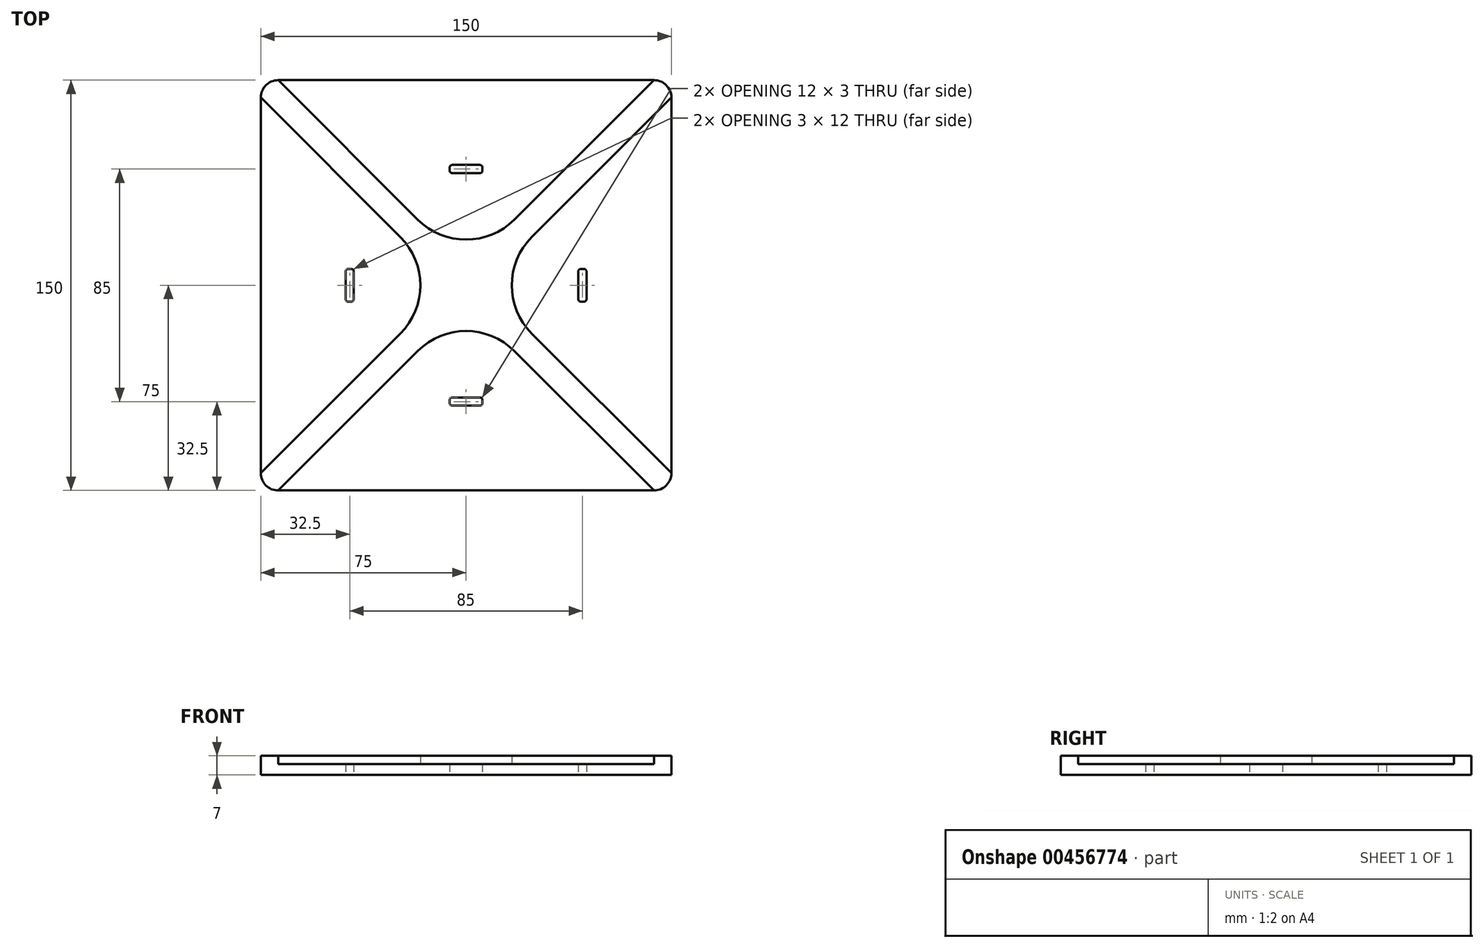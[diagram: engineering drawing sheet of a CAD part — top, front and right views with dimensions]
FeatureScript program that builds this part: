
annotation { "Feature Type Name" : "Feature", "Feature Type Description" : "" }
export const myFeature = defineFeature(function(context is Context, id is Id, definition is map)
    precondition{}
    {
        {
            var Q0;
            Q0=qCreatedBy(makeId("Top.planeOp"),FACE);
            var sketch = newSketch(context, id + "F0", { "sketchPlane" : qUnion([Q0])});
            skLineSegment(sketch, "E0.bottom", {"start": v(68.65, 75) * mm, "end": v(-68.65, 75) * mm});
            skLineSegment(sketch, "E0.top", {"start": v(68.65, -75) * mm, "end": v(-68.65, -75) * mm});
            skLineSegment(sketch, "E0.left", {"start": v(75, 68.65) * mm, "end": v(75, -68.65) * mm});
            skLineSegment(sketch, "E0.right", {"start": v(-75, 68.65) * mm, "end": v(-75, -68.65) * mm});
            skPoint(sketch, "E0.middle", {"position": v(0, 0) * mm});
            skPoint(sketch, "E1", {"position": v(0, 42.5) * mm});
            skLineSegment(sketch, "E2.bottom", {"start": v(5.02, 44) * mm, "end": v(-5.02, 44) * mm});
            skLineSegment(sketch, "E2.top", {"start": v(5.02, 41) * mm, "end": v(-5.02, 41) * mm});
            skLineSegment(sketch, "E2.left", {"start": v(6, 43.02) * mm, "end": v(6, 41.98) * mm});
            skLineSegment(sketch, "E2.right", {"start": v(-6, 43.02) * mm, "end": v(-6, 41.98) * mm});
            skPoint(sketch, "E3.MirrorP", {"position": v(0, -42.5) * mm});
            skLineSegment(sketch, "E4.MirrorCS", {"start": v(5.02, -44) * mm, "end": v(-5.02, -44) * mm});
            skLineSegment(sketch, "E5.MirrorCS", {"start": v(-6, -43.02) * mm, "end": v(-6, -41.98) * mm});
            skLineSegment(sketch, "E6.MirrorCS", {"start": v(6, -43.02) * mm, "end": v(6, -41.98) * mm});
            skLineSegment(sketch, "E7.MirrorCS", {"start": v(5.02, -41) * mm, "end": v(-5.02, -41) * mm});
            skPoint(sketch, "E8.2.0", {"position": v(42.5, 0) * mm});
            skLineSegment(sketch, "E8.2.1", {"start": v(44, 5.02) * mm, "end": v(44, -5.02) * mm});
            skLineSegment(sketch, "E8.2.2", {"start": v(43.02, -6) * mm, "end": v(41.98, -6) * mm});
            skLineSegment(sketch, "E8.2.3", {"start": v(43.02, 6) * mm, "end": v(41.98, 6) * mm});
            skLineSegment(sketch, "E8.2.4", {"start": v(41, 5.02) * mm, "end": v(41, -5.02) * mm});
            skPoint(sketch, "E8.2.5", {"position": v(42.5, 0) * mm});
            skPoint(sketch, "E8.2.6", {"position": v(42.5, 0) * mm});
            skPoint(sketch, "E9.2.0", {"position": v(-42.5, 0) * mm});
            skLineSegment(sketch, "E9.2.1", {"start": v(-41, -5.02) * mm, "end": v(-41, 5.02) * mm});
            skLineSegment(sketch, "E9.2.2", {"start": v(-43.02, -6) * mm, "end": v(-41.98, -6) * mm});
            skLineSegment(sketch, "E9.2.3", {"start": v(-43.02, 6) * mm, "end": v(-41.98, 6) * mm});
            skLineSegment(sketch, "E9.2.4", {"start": v(-44, -5.02) * mm, "end": v(-44, 5.02) * mm});
            skPoint(sketch, "E9.2.5", {"position": v(-42.5, 0) * mm});
            skPoint(sketch, "E9.2.6", {"position": v(-42.5, 0) * mm});
            skPoint(sketch, "E10.visualSharp", {"position": v(-75, 75) * mm});
            skArc(sketch, "E10.filletArc", {"start": v(-68.65, 75) * mm, "mid": v(-73.14, 73.14) * mm, "end": v(-75, 68.65) * mm});
            skPoint(sketch, "E11.visualSharp", {"position": v(75, 75) * mm});
            skArc(sketch, "E11.filletArc", {"start": v(75, 68.65) * mm, "mid": v(73.14, 73.14) * mm, "end": v(68.65, 75) * mm});
            skPoint(sketch, "E12.visualSharp", {"position": v(75, -75) * mm});
            skArc(sketch, "E12.filletArc", {"start": v(68.65, -75) * mm, "mid": v(73.14, -73.14) * mm, "end": v(75, -68.65) * mm});
            skPoint(sketch, "E13.visualSharp", {"position": v(-75, -75) * mm});
            skArc(sketch, "E13.filletArc", {"start": v(-75, -68.65) * mm, "mid": v(-73.14, -73.14) * mm, "end": v(-68.65, -75) * mm});
            skPoint(sketch, "E14.visualSharp", {"position": v(-6, 44) * mm});
            skArc(sketch, "E14.filletArc", {"start": v(-5.02, 44) * mm, "mid": v(-5.71, 43.71) * mm, "end": v(-6, 43.02) * mm});
            skPoint(sketch, "E15.visualSharp", {"position": v(-6, 41) * mm});
            skArc(sketch, "E15.filletArc", {"start": v(-6, 41.98) * mm, "mid": v(-5.71, 41.29) * mm, "end": v(-5.02, 41) * mm});
            skPoint(sketch, "E16.visualSharp", {"position": v(6, 41) * mm});
            skArc(sketch, "E16.filletArc", {"start": v(5.02, 41) * mm, "mid": v(5.71, 41.29) * mm, "end": v(6, 41.98) * mm});
            skPoint(sketch, "E17.visualSharp", {"position": v(6, 44) * mm});
            skArc(sketch, "E17.filletArc", {"start": v(6, 43.02) * mm, "mid": v(5.71, 43.71) * mm, "end": v(5.02, 44) * mm});
            skPoint(sketch, "E18.visualSharp", {"position": v(41, 6) * mm});
            skArc(sketch, "E18.filletArc", {"start": v(41.98, 6) * mm, "mid": v(41.29, 5.71) * mm, "end": v(41, 5.02) * mm});
            skPoint(sketch, "E19.visualSharp", {"position": v(44, 6) * mm});
            skArc(sketch, "E19.filletArc", {"start": v(44, 5.02) * mm, "mid": v(43.71, 5.71) * mm, "end": v(43.02, 6) * mm});
            skPoint(sketch, "E20.visualSharp", {"position": v(41, -6) * mm});
            skArc(sketch, "E20.filletArc", {"start": v(41, -5.02) * mm, "mid": v(41.29, -5.71) * mm, "end": v(41.98, -6) * mm});
            skPoint(sketch, "E21.visualSharp", {"position": v(44, -6) * mm});
            skArc(sketch, "E21.filletArc", {"start": v(43.02, -6) * mm, "mid": v(43.71, -5.71) * mm, "end": v(44, -5.02) * mm});
            skPoint(sketch, "E22.visualSharp", {"position": v(6, -41) * mm});
            skArc(sketch, "E22.filletArc", {"start": v(6, -41.98) * mm, "mid": v(5.71, -41.29) * mm, "end": v(5.02, -41) * mm});
            skPoint(sketch, "E23.visualSharp", {"position": v(6, -44) * mm});
            skArc(sketch, "E23.filletArc", {"start": v(5.02, -44) * mm, "mid": v(5.71, -43.71) * mm, "end": v(6, -43.02) * mm});
            skPoint(sketch, "E24.visualSharp", {"position": v(-6, -44) * mm});
            skArc(sketch, "E24.filletArc", {"start": v(-6, -43.02) * mm, "mid": v(-5.71, -43.71) * mm, "end": v(-5.02, -44) * mm});
            skPoint(sketch, "E25.visualSharp", {"position": v(-6, -41) * mm});
            skArc(sketch, "E25.filletArc", {"start": v(-5.02, -41) * mm, "mid": v(-5.71, -41.29) * mm, "end": v(-6, -41.98) * mm});
            skPoint(sketch, "E26.visualSharp", {"position": v(-41, 6) * mm});
            skArc(sketch, "E26.filletArc", {"start": v(-41, 5.02) * mm, "mid": v(-41.29, 5.71) * mm, "end": v(-41.98, 6) * mm});
            skPoint(sketch, "E27.visualSharp", {"position": v(-41, -6) * mm});
            skArc(sketch, "E27.filletArc", {"start": v(-41.98, -6) * mm, "mid": v(-41.29, -5.71) * mm, "end": v(-41, -5.02) * mm});
            skPoint(sketch, "E28.visualSharp", {"position": v(-44, -6) * mm});
            skArc(sketch, "E28.filletArc", {"start": v(-44, -5.02) * mm, "mid": v(-43.71, -5.71) * mm, "end": v(-43.02, -6) * mm});
            skPoint(sketch, "E29.visualSharp", {"position": v(-44, 6) * mm});
            skArc(sketch, "E29.filletArc", {"start": v(-43.02, 6) * mm, "mid": v(-43.71, 5.71) * mm, "end": v(-44, 5.02) * mm});
            skLineSegment(sketch, "E30", {"start": v(-68.65, -75) * mm, "end": v(-17.68, -24.03) * mm});
            skLineSegment(sketch, "E31", {"start": v(-75, -68.65) * mm, "end": v(-24.03, -17.68) * mm});
            skLineSegment(sketch, "E32", {"start": v(68.65, -75) * mm, "end": v(17.68, -24.03) * mm});
            skLineSegment(sketch, "E33", {"start": v(-68.65, 75) * mm, "end": v(-17.68, 24.03) * mm});
            skLineSegment(sketch, "E34.trimOffspring", {"start": v(24.03, 17.68) * mm, "end": v(75, 68.65) * mm});
            skLineSegment(sketch, "E35.trimOffspring", {"start": v(-24.03, 17.68) * mm, "end": v(-75, 68.65) * mm});
            skLineSegment(sketch, "E36.trimOffspring", {"start": v(17.68, 24.03) * mm, "end": v(68.65, 75) * mm});
            skLineSegment(sketch, "E37.trimOffspring", {"start": v(24.03, -17.68) * mm, "end": v(75, -68.65) * mm});
            skPoint(sketch, "E38.visualSharp", {"position": v(0, -6.35) * mm});
            skArc(sketch, "E38.filletArc", {"start": v(17.68, -24.03) * mm, "mid": v(0, -16.7) * mm, "end": v(-17.68, -24.03) * mm});
            skPoint(sketch, "E39.visualSharp", {"position": v(-6.35, 0) * mm});
            skArc(sketch, "E39.filletArc", {"start": v(-24.03, -17.68) * mm, "mid": v(-16.7, 0) * mm, "end": v(-24.03, 17.68) * mm});
            skPoint(sketch, "E40.visualSharp", {"position": v(0, 6.35) * mm});
            skArc(sketch, "E40.filletArc", {"start": v(-17.68, 24.03) * mm, "mid": v(0, 16.7) * mm, "end": v(17.68, 24.03) * mm});
            skPoint(sketch, "E41.visualSharp", {"position": v(6.35, 0) * mm});
            skArc(sketch, "E41.filletArc", {"start": v(24.03, 17.68) * mm, "mid": v(16.7, 0) * mm, "end": v(24.03, -17.68) * mm});
            skSolve(sketch);
        }
        {
            var Q0;
            Q0=makeQuery(id+"F0.imprint","IMPRINT",FACE,{"disambiguationData":[TD([[makeQuery(id+"F0.imprint","IMPRINT",EDGE,{"derivedFrom":sQuery(id+"F0.wireOp",EDGE,"E10.filletArc")}),1.0]])]});
            extrude(context, id + "F1", {"entities" : qUnion([Q0]), "depth" : 7 * mm});
        }
        {
            var Q0;
            Q0 = qSketchRegion(id + "F0", true);
            extrude(context, id + "F2", {"entities" : qUnion([Q0]), "operationType" : NewBodyOperationType.ADD, "depth" : 4 * mm});
        }
    });
